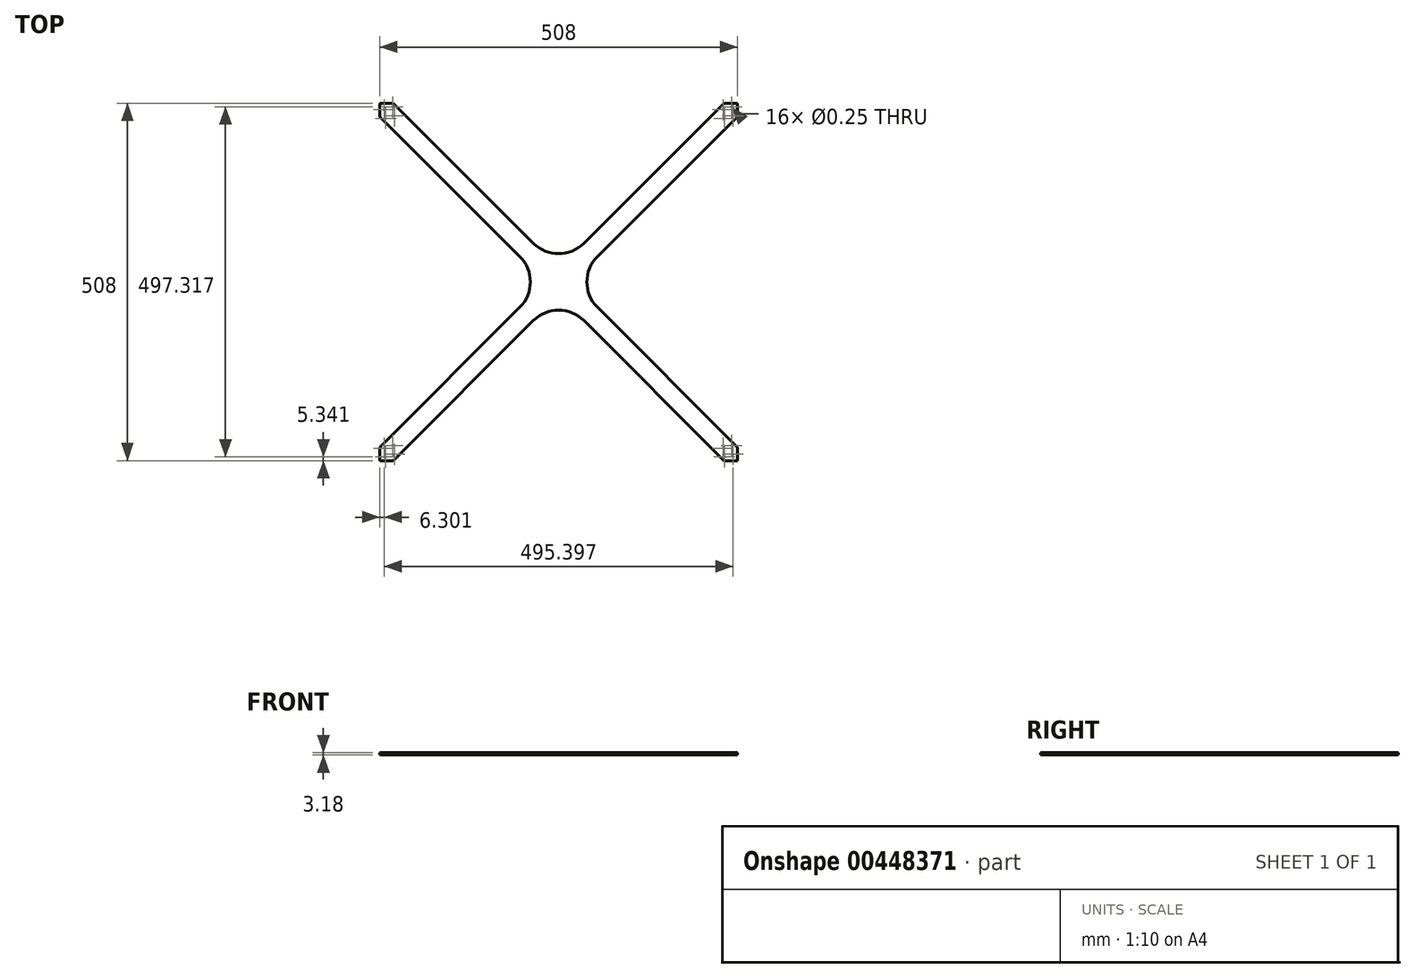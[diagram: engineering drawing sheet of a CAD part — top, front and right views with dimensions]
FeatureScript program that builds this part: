
annotation { "Feature Type Name" : "Feature", "Feature Type Description" : "" }
export const myFeature = defineFeature(function(context is Context, id is Id, definition is map)
    precondition{}
    {
        {
            var Q0;
            Q0=qCreatedBy(makeId("Top.planeOp"),FACE);
            var sketch = newSketch(context, id + "F0", { "sketchPlane" : qUnion([Q0])});
            skLineSegment(sketch, "E0.bottom", {"start": v(254, 254) * mm, "end": v(-254, 254) * mm});
            skLineSegment(sketch, "E0.top", {"start": v(254, -254) * mm, "end": v(-254, -254) * mm});
            skLineSegment(sketch, "E0.left", {"start": v(254, 254) * mm, "end": v(254, -254) * mm});
            skLineSegment(sketch, "E0.right", {"start": v(-254, 254) * mm, "end": v(-254, -254) * mm});
            skPoint(sketch, "E0.middle", {"position": v(0, 0) * mm});
            skSolve(sketch);
        }
        {
            var Q0;
            Q0=makeQuery(id+"F0.imprint","IMPRINT",FACE,{"disambiguationData":[TD([[makeQuery(id+"F0.imprint","IMPRINT",EDGE,{"derivedFrom":sQuery(id+"F0.wireOp",EDGE,"E0.bottom")}),1.0]])]});
            extrude(context, id + "F1", {"entities" : qUnion([Q0]), "depth" : 3.17 * mm});
        }
        {
            var Q0;
            Q0=makeQuery(id+"F1.opExtrude","CAP_FACE",FACE,{"disambiguationData":[OSD([sQuery(id+"F0.wireOp",EDGE,"E0.bottom"),sQuery(id+"F0.wireOp",EDGE,"E0.top"),sQuery(id+"F0.wireOp",EDGE,"E0.left"),sQuery(id+"F0.wireOp",EDGE,"E0.right")])],"isStart":false});
            var sketch = newSketch(context, id + "F2", { "sketchPlane" : qUnion([Q0])});
            skLineSegment(sketch, "E1", {"start": v(0, 19.05) * mm, "end": v(234.95, 254) * mm});
            skLineSegment(sketch, "E2", {"start": v(19.05, 0) * mm, "end": v(254, 234.95) * mm});
            skLineSegment(sketch, "E3.MirrorCS", {"start": v(0, 19.05) * mm, "end": v(-234.95, 254) * mm});
            skLineSegment(sketch, "E4.MirrorCS", {"start": v(-19.05, 0) * mm, "end": v(-254, 234.95) * mm});
            skLineSegment(sketch, "E5.MirrorCS", {"start": v(19.05, 0) * mm, "end": v(254, -234.95) * mm});
            skLineSegment(sketch, "E6.MirrorCS", {"start": v(-19.05, 0) * mm, "end": v(-254, -234.95) * mm});
            skLineSegment(sketch, "E7.MirrorCS", {"start": v(0, -19.05) * mm, "end": v(-234.95, -254) * mm});
            skLineSegment(sketch, "E8.MirrorCS", {"start": v(0, -19.05) * mm, "end": v(234.95, -254) * mm});
            skLineSegment(sketch, "E9", {"start": v(-234.95, 254) * mm, "end": v(234.95, 254) * mm});
            skLineSegment(sketch, "E10", {"start": v(254, 234.95) * mm, "end": v(254, -234.95) * mm});
            skLineSegment(sketch, "E11", {"start": v(-254, -234.95) * mm, "end": v(-254, 234.95) * mm});
            skLineSegment(sketch, "E12", {"start": v(-234.95, -254) * mm, "end": v(234.95, -254) * mm});
            skLineSegment(sketch, "E13", {"start": v(0, 0) * mm, "end": v(254, -254) * mm});
            skSolve(sketch);
        }
        {
            var Q0;
            Q0=makeQuery(id+"F2.imprint","IMPRINT",FACE,{"disambiguationData":[TD([[makeQuery(id+"F2.imprint","IMPRINT",EDGE,{"derivedFrom":sQuery(id+"F2.wireOp",EDGE,"E4.MirrorCS")}),1.0]])]});
            var Q1;
            Q1=makeQuery(id+"F2.imprint","IMPRINT",FACE,{"disambiguationData":[TD([[makeQuery(id+"F2.imprint","IMPRINT",EDGE,{"derivedFrom":sQuery(id+"F2.wireOp",EDGE,"E1")}),1.0]])]});
            var Q2;
            Q2=makeQuery(id+"F2.imprint","IMPRINT",FACE,{"disambiguationData":[TD([[makeQuery(id+"F2.imprint","IMPRINT",EDGE,{"derivedFrom":sQuery(id+"F2.wireOp",EDGE,"E2")}),-1.0]])]});
            var Q3;
            Q3=makeQuery(id+"F2.imprint","IMPRINT",FACE,{"disambiguationData":[TD([[makeQuery(id+"F2.imprint","IMPRINT",EDGE,{"derivedFrom":sQuery(id+"F2.wireOp",EDGE,"E7.MirrorCS")}),1.0]])]});
            extrude(context, id + "F3", {"entities" : qUnion([Q0, Q1, Q2, Q3]), "operationType" : NewBodyOperationType.REMOVE, "endBound" : BoundingType.THROUGH_ALL, "oppositeDirection" : true, "depth" : 25.4 * mm});
        }
        {
            var Q0;
            Q0=makeQuery(id+"F3.boolean.opBoolean","COPY",EDGE,{"derivedFrom":makeQuery(id+"F3.opExtrude","SWEPT_EDGE",EDGE,{"disambiguationData":[OSD([sQuery(id+"F2.wireOp",EDGE,"E4.MirrorCS"),sQuery(id+"F2.wireOp",EDGE,"E6.MirrorCS")])]})});
            var Q1;
            Q1=makeQuery(id+"F3.boolean.opBoolean","COPY",EDGE,{"derivedFrom":makeQuery(id+"F3.opExtrude","SWEPT_EDGE",EDGE,{"disambiguationData":[OSD([sQuery(id+"F2.wireOp",EDGE,"E7.MirrorCS"),sQuery(id+"F2.wireOp",EDGE,"E8.MirrorCS")])]})});
            var Q2;
            Q2=makeQuery(id+"F3.boolean.opBoolean","COPY",EDGE,{"derivedFrom":makeQuery(id+"F3.opExtrude","SWEPT_EDGE",EDGE,{"disambiguationData":[OSD([sQuery(id+"F2.wireOp",EDGE,"E2"),sQuery(id+"F2.wireOp",EDGE,"E5.MirrorCS")])]})});
            var Q3;
            Q3=makeQuery(id+"F3.boolean.opBoolean","COPY",EDGE,{"derivedFrom":makeQuery(id+"F3.opExtrude","SWEPT_EDGE",EDGE,{"disambiguationData":[OSD([sQuery(id+"F2.wireOp",EDGE,"E1"),sQuery(id+"F2.wireOp",EDGE,"E3.MirrorCS")])]})});
            fillet(context, id + "F4", {"entities" : qUnion([Q0, Q1, Q2, Q3]), "radius" : 50.8 * mm, "tangentPropagation" : true, "allowEdgeOverflow" : false});
        }
        {
            var Q0;
            Q0=makeQuery(id+"F1.opExtrude","CAP_FACE",FACE,{"disambiguationData":[OSD([sQuery(id+"F0.wireOp",EDGE,"E0.bottom"),sQuery(id+"F0.wireOp",EDGE,"E0.top"),sQuery(id+"F0.wireOp",EDGE,"E0.left"),sQuery(id+"F0.wireOp",EDGE,"E0.right")])],"isStart":true});
            var sketch = newSketch(context, id + "F5", { "sketchPlane" : qUnion([Q0])});
            skLineSegment(sketch, "E14", {"start": v(-40.1, 0) * mm, "end": v(40.1, 0) * mm});
            skLineSegment(sketch, "E15", {"start": v(0, 40.1) * mm, "end": v(0, -40.1) * mm});
            skLineSegment(sketch, "E16", {"start": v(0, 0) * mm, "end": v(-254, -254) * mm});
            skLineSegment(sketch, "E17", {"start": v(0, 0) * mm, "end": v(254, -254) * mm});
            skLineSegment(sketch, "E18", {"start": v(0, 0) * mm, "end": v(254, 254) * mm});
            skLineSegment(sketch, "E19", {"start": v(234.95, -254) * mm, "end": v(254, -234.95) * mm});
            skLineSegment(sketch, "E20", {"start": v(-254, -234.95) * mm, "end": v(-234.95, -254) * mm});
            skLineSegment(sketch, "E21", {"start": v(234.95, 254) * mm, "end": v(254, 234.95) * mm});
            skLineSegment(sketch, "E22", {"start": v(-254, 234.95) * mm, "end": v(-234.95, 254) * mm});
            skCircle(sketch, "E23", {"center": v(-125.31, -108.96) * mm, "radius": 1.59 * mm});
            skLineSegment(sketch, "E24", {"start": v(247.7, -236.15) * mm, "end": v(235.57, -232.4) * mm});
            skLineSegment(sketch, "E25", {"start": v(247.7, -236.15) * mm, "end": v(245.5, -248.66) * mm});
            skLineSegment(sketch, "E26", {"start": v(235.57, -232.4) * mm, "end": v(233.36, -244.9) * mm});
            skLineSegment(sketch, "E27", {"start": v(233.36, -244.9) * mm, "end": v(245.5, -248.66) * mm});
            skLineSegment(sketch, "E28", {"start": v(245.5, -248.66) * mm, "end": v(235.57, -232.4) * mm});
            skPoint(sketch, "E29.endSnap0", {"position": v(240.53, -240.53) * mm});
            skPoint(sketch, "E30.endSnap0", {"position": v(-240.53, -240.53) * mm});
            skLineSegment(sketch, "E31", {"start": v(247.7, 244.9) * mm, "end": v(235.57, 248.66) * mm});
            skLineSegment(sketch, "E32", {"start": v(247.7, 244.9) * mm, "end": v(245.5, 232.4) * mm});
            skLineSegment(sketch, "E33", {"start": v(235.57, 248.66) * mm, "end": v(233.36, 236.15) * mm});
            skLineSegment(sketch, "E34", {"start": v(233.36, 236.15) * mm, "end": v(245.5, 232.4) * mm});
            skLineSegment(sketch, "E35", {"start": v(245.5, 232.4) * mm, "end": v(235.57, 248.66) * mm});
            skPoint(sketch, "E36.endSnap0", {"position": v(240.53, 240.53) * mm});
            skLineSegment(sketch, "E37", {"start": v(-233.36, 244.9) * mm, "end": v(-245.5, 248.66) * mm});
            skLineSegment(sketch, "E38", {"start": v(-233.36, 244.9) * mm, "end": v(-235.57, 232.4) * mm});
            skLineSegment(sketch, "E39", {"start": v(-245.5, 248.66) * mm, "end": v(-247.7, 236.15) * mm});
            skLineSegment(sketch, "E40", {"start": v(-247.7, 236.15) * mm, "end": v(-235.57, 232.4) * mm});
            skLineSegment(sketch, "E41", {"start": v(-235.57, 232.4) * mm, "end": v(-245.5, 248.66) * mm});
            skPoint(sketch, "E42.endSnap0", {"position": v(-240.53, 240.53) * mm});
            skLineSegment(sketch, "E43", {"start": v(-254, 254) * mm, "end": v(0, 0) * mm});
            skCircle(sketch, "E44", {"center": v(0, -23.16) * mm, "radius": 3.18 * mm});
            skCircle(sketch, "E45", {"center": v(0, 19.8) * mm, "radius": 3.18 * mm});
            skPoint(sketch, "E46", {"position": v(-247.7, 236.15) * mm});
            skPoint(sketch, "E47", {"position": v(-245.5, 248.66) * mm});
            skPoint(sketch, "E48", {"position": v(-233.36, 244.9) * mm});
            skPoint(sketch, "E49", {"position": v(-235.57, 232.4) * mm});
            skPoint(sketch, "E50", {"position": v(-247.7, -244.9) * mm});
            skPoint(sketch, "E51", {"position": v(-245.5, -232.4) * mm});
            skPoint(sketch, "E52", {"position": v(-233.36, -236.15) * mm});
            skPoint(sketch, "E53", {"position": v(-235.57, -248.66) * mm});
            skPoint(sketch, "E54", {"position": v(235.57, -232.4) * mm});
            skPoint(sketch, "E55", {"position": v(233.36, -244.9) * mm});
            skPoint(sketch, "E56", {"position": v(245.5, -248.66) * mm});
            skPoint(sketch, "E57", {"position": v(247.7, -236.15) * mm});
            skPoint(sketch, "E58", {"position": v(233.36, 236.15) * mm});
            skPoint(sketch, "E59", {"position": v(235.57, 248.66) * mm});
            skPoint(sketch, "E60", {"position": v(247.7, 244.9) * mm});
            skPoint(sketch, "E61", {"position": v(245.5, 232.4) * mm});
            skSolve(sketch);
        }
        {
            var Q0;
            Q0=sQuery(id+"F5.wireOp",VERTEX,"E50");
            var Q1;
            Q1=sQuery(id+"F5.wireOp",VERTEX,"E51");
            var Q2;
            Q2=sQuery(id+"F5.wireOp",VERTEX,"E52");
            var Q3;
            Q3=sQuery(id+"F5.wireOp",VERTEX,"E53");
            var Q4;
            Q4=sQuery(id+"F5.wireOp",VERTEX,"E47");
            var Q5;
            Q5=sQuery(id+"F5.wireOp",VERTEX,"E48");
            var Q6;
            Q6=sQuery(id+"F5.wireOp",VERTEX,"E49");
            var Q7;
            Q7=sQuery(id+"F5.wireOp",VERTEX,"E46");
            var Q8;
            Q8=sQuery(id+"F5.wireOp",VERTEX,"E55");
            var Q9;
            Q9=sQuery(id+"F5.wireOp",VERTEX,"E56");
            var Q10;
            Q10=sQuery(id+"F5.wireOp",VERTEX,"E57");
            var Q11;
            Q11=sQuery(id+"F5.wireOp",VERTEX,"E54");
            var Q12;
            Q12=sQuery(id+"F5.wireOp",VERTEX,"E61");
            var Q13;
            Q13=sQuery(id+"F5.wireOp",VERTEX,"E58");
            var Q14;
            Q14=sQuery(id+"F5.wireOp",VERTEX,"E59");
            var Q15;
            Q15=sQuery(id+"F5.wireOp",VERTEX,"E60");
            var Q16;
            Q16=makeQuery(id+"F1.opExtrude","SWEPT_BODY",BODY,{"disambiguationData":[OSD([sQuery(id+"F0.wireOp",EDGE,"E0.bottom"),sQuery(id+"F0.wireOp",EDGE,"E0.top"),sQuery(id+"F0.wireOp",EDGE,"E0.left"),sQuery(id+"F0.wireOp",EDGE,"E0.right")])]});
            hole(context, id + "F6", {"style" : HoleStyle.SIMPLE, "endStyle" : HoleEndStyle.THROUGH, "holeDiameter" : 0.25 * mm, "tappedDepth" : 12.7 * mm, "tapClearance" : 3, "locations" : qUnion([Q0, Q1, Q2, Q3, Q4, Q5, Q6, Q7, Q8, Q9, Q10, Q11, Q12, Q13, Q14, Q15]), "scope" : qUnion([Q16])});
        }
    });
